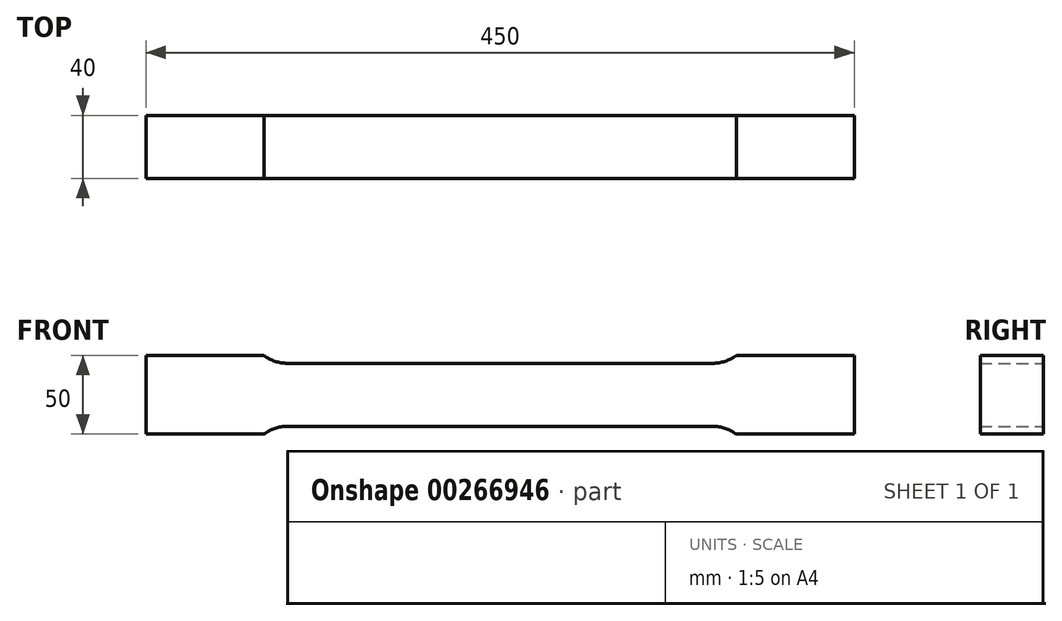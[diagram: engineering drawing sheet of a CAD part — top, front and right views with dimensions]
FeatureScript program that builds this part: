
annotation { "Feature Type Name" : "Feature", "Feature Type Description" : "" }
export const myFeature = defineFeature(function(context is Context, id is Id, definition is map)
    precondition{}
    {
        {
            var Q0;
            Q0=qCreatedBy(makeId("Front.planeOp"),FACE);
            var sketch = newSketch(context, id + "F0", { "sketchPlane" : qUnion([Q0])});
            skLineSegment(sketch, "E0", {"start": v(0, 20) * mm, "end": v(135, 20) * mm});
            skArc(sketch, "E1", {"start": v(135, 20) * mm, "mid": v(142.9, 21.28) * mm, "end": v(150, 25) * mm});
            skLineSegment(sketch, "E2", {"start": v(150, 25) * mm, "end": v(225, 25) * mm});
            skLineSegment(sketch, "E3", {"start": v(225, 25) * mm, "end": v(225, 0) * mm});
            skLineSegment(sketch, "E4.MirrorCS", {"start": v(0, -20) * mm, "end": v(135, -20) * mm});
            skLineSegment(sketch, "E5.MirrorCS", {"start": v(225, -25) * mm, "end": v(225, 0) * mm});
            skLineSegment(sketch, "E6.MirrorCS", {"start": v(150, -25) * mm, "end": v(225, -25) * mm});
            skArc(sketch, "E7.MirrorCS", {"start": v(135, -20) * mm, "mid": v(142.9, -21.28) * mm, "end": v(150, -25) * mm});
            skArc(sketch, "E8.MirrorCS", {"start": v(-135, -20) * mm, "mid": v(-142.9, -21.28) * mm, "end": v(-150, -25) * mm});
            skLineSegment(sketch, "E9.MirrorCS", {"start": v(-150, -25) * mm, "end": v(-225, -25) * mm});
            skArc(sketch, "E10.MirrorCS", {"start": v(-135, 20) * mm, "mid": v(-142.9, 21.28) * mm, "end": v(-150, 25) * mm});
            skLineSegment(sketch, "E11.MirrorCS", {"start": v(-150, 25) * mm, "end": v(-225, 25) * mm});
            skLineSegment(sketch, "E12.MirrorCS", {"start": v(-225, -25) * mm, "end": v(-225, 0) * mm});
            skLineSegment(sketch, "E13.MirrorCS", {"start": v(0, -20) * mm, "end": v(-135, -20) * mm});
            skLineSegment(sketch, "E14.MirrorCS", {"start": v(-225, 25) * mm, "end": v(-225, 0) * mm});
            skLineSegment(sketch, "E15.MirrorCS", {"start": v(0, 20) * mm, "end": v(-135, 20) * mm});
            skSolve(sketch);
        }
        {
            var Q0;
            Q0 = qSketchRegion(id + "F0", true);
            extrude(context, id + "F1", {"entities" : qUnion([Q0]), "endBound" : BoundingType.SYMMETRIC, "depth" : 40 * mm});
        }
    });
